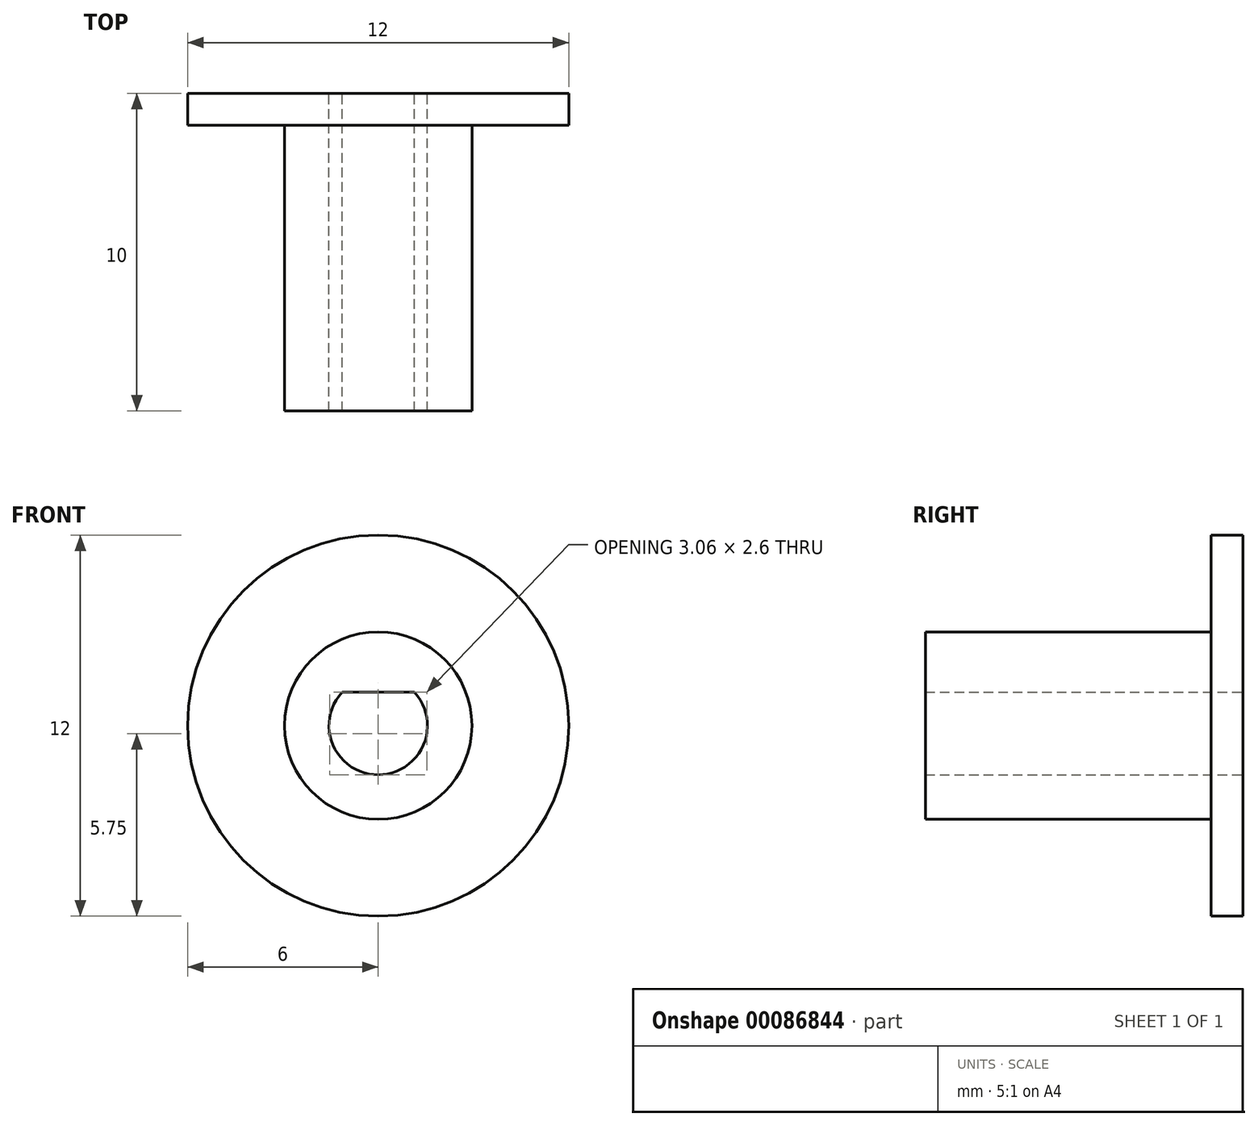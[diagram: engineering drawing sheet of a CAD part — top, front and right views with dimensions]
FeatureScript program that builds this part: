
annotation { "Feature Type Name" : "Feature", "Feature Type Description" : "" }
export const myFeature = defineFeature(function(context is Context, id is Id, definition is map)
    precondition{}
    {
        {
            var Q0;
            Q0=qCreatedBy(makeId("Front.planeOp"),FACE);
            var sketch = newSketch(context, id + "F0", { "sketchPlane" : qUnion([Q0])});
            skCircle(sketch, "E0", {"center": v(0, 0) * mm, "radius": 6 * mm});
            skLineSegment(sketch, "E1", {"start": v(-1.14, 1.05) * mm, "end": v(1.14, 1.05) * mm});
            skArc(sketch, "E2", {"start": v(-1.14, 1.05) * mm, "mid": v(0, -1.55) * mm, "end": v(1.14, 1.05) * mm});
            skCircle(sketch, "E3", {"center": v(0, 0) * mm, "radius": 2.95 * mm});
            skSolve(sketch);
        }
        {
            var Q0;
            Q0=makeQuery(id+"F0.imprint","IMPRINT",FACE,{"disambiguationData":[TD([[makeQuery(id+"F0.imprint","IMPRINT",EDGE,{"derivedFrom":sQuery(id+"F0.wireOp",EDGE,"E1")}),1.0]])]});
            extrude(context, id + "F1", {"entities" : qUnion([Q0]), "depth" : 10 * mm, "offsetDistance" : 25 * mm});
        }
        {
            var Q0;
            Q0=makeQuery(id+"F0.imprint","IMPRINT",FACE,{"disambiguationData":[TD([[makeQuery(id+"F0.imprint","IMPRINT",EDGE,{"derivedFrom":sQuery(id+"F0.wireOp",EDGE,"E0")}),1.0]])]});
            extrude(context, id + "F2", {"entities" : qUnion([Q0]), "operationType" : NewBodyOperationType.ADD, "depth" : 1 * mm, "offsetDistance" : 25 * mm});
        }
    });
